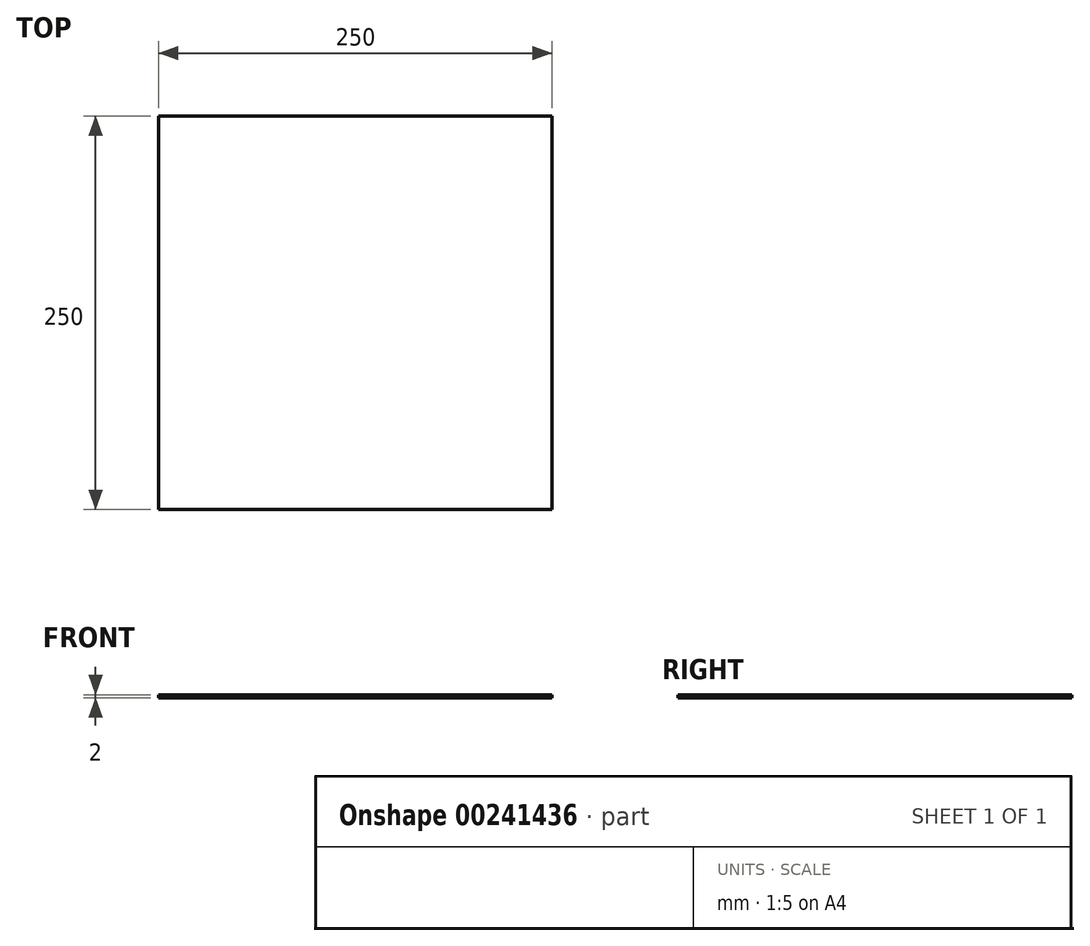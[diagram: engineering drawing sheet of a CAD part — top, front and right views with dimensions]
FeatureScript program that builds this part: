
annotation { "Feature Type Name" : "Feature", "Feature Type Description" : "" }
export const myFeature = defineFeature(function(context is Context, id is Id, definition is map)
    precondition{}
    {
        {
            var Q0;
            Q0=qCreatedBy(makeId("Top.planeOp"),FACE);
            var sketch = newSketch(context, id + "F0", { "sketchPlane" : qUnion([Q0])});
            skLineSegment(sketch, "E0.bottom", {"start": v(-125, 125) * mm, "end": v(125, 125) * mm});
            skLineSegment(sketch, "E0.top", {"start": v(-125, -125) * mm, "end": v(125, -125) * mm});
            skLineSegment(sketch, "E0.left", {"start": v(-125, 125) * mm, "end": v(-125, -125) * mm});
            skLineSegment(sketch, "E0.right", {"start": v(125, 125) * mm, "end": v(125, -125) * mm});
            skPoint(sketch, "E0.middle", {"position": v(0, 0) * mm});
            skSolve(sketch);
        }
        {
            var Q0;
            Q0 = qSketchRegion(id + "F0", true);
            extrude(context, id + "F1", {"entities" : qUnion([Q0]), "depth" : 2 * mm});
        }
    });
